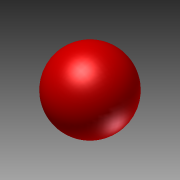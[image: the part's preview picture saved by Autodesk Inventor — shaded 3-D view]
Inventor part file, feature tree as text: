
AUTODESK INVENTOR PART (.ipt)
format: ipt  version: 2012 (Build 160160000, 160)  size: 102,912 bytes
history: native  units: in
note: dims shown in document units (in); Inventor stores cm internally (conversion verified against a paired STEP export)
features: extrude x1, fillet x1, sketch x1
ambient origin geometry x8: Origin, YZ Plane, XZ Plane, XY Plane, X Axis, Y Axis, Z Axis, Center Point
bodies: Solid1 (feature_tree)
feature tree (3):
  extrude  "Extrusion1"  Depth=6.3in TaperAngle=0.0deg
  fillet  "Fillet1"  Radius=3.15in
  sketch  "Sketch1"  dims[d0=6.3in d1=6.3in d2=0.0in d3=3.15in]
